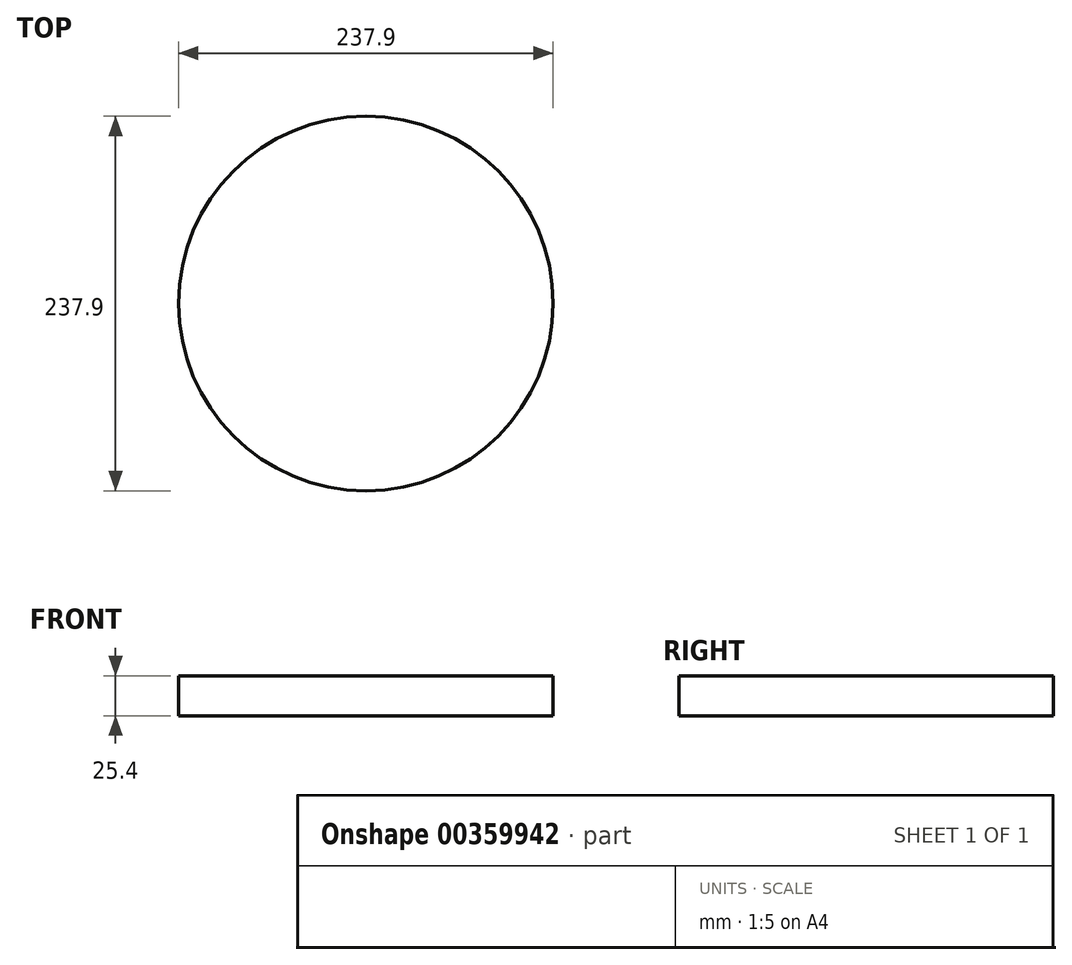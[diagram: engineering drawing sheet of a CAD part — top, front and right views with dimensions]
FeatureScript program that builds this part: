
annotation { "Feature Type Name" : "Feature", "Feature Type Description" : "" }
export const myFeature = defineFeature(function(context is Context, id is Id, definition is map)
    precondition{}
    {
        {
            var Q0;
            Q0=qCreatedBy(makeId("Top.planeOp"),FACE);
            var sketch = newSketch(context, id + "F0", { "sketchPlane" : qUnion([Q0])});
            skCircle(sketch, "E0", {"center": v(0, 0) * mm, "radius": 118.95 * mm});
            skSolve(sketch);
        }
        {
            var Q0;
            Q0 = qSketchRegion(id + "F0", true);
            extrude(context, id + "F1", {"entities" : qUnion([Q0]), "depth" : 25.4 * mm});
        }
    });
